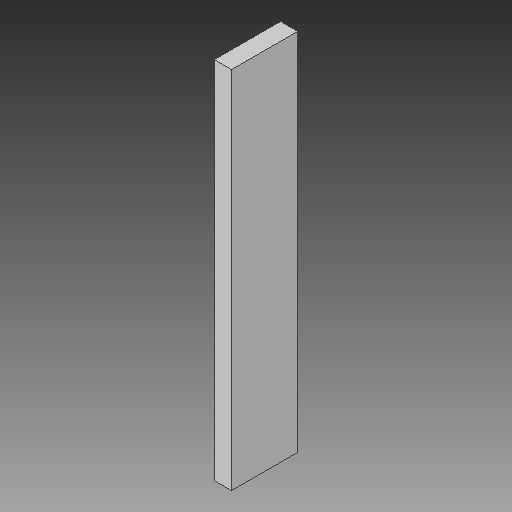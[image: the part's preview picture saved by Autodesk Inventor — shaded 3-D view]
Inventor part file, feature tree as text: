
AUTODESK INVENTOR PART (.ipt)
format: ipt  version: 2019 (Build 230136000, 136)  size: 90,624 bytes
history: native  units: in
note: dims shown in document units (in); Inventor stores cm internally (conversion verified against a paired STEP export)
features: extrude x1, sketch x1
ambient origin geometry x8: Origin, YZ Plane, XZ Plane, XY Plane, X Axis, Y Axis, Z Axis, Center Point
bodies: Solid1 (feature_tree)
feature tree (2):
  extrude  "Extrusion1"  Depth=1.5in
  sketch  "Sketch1"  dims[d0=8.25in d1=1.5in d2=0.39in d3=0.0in]
